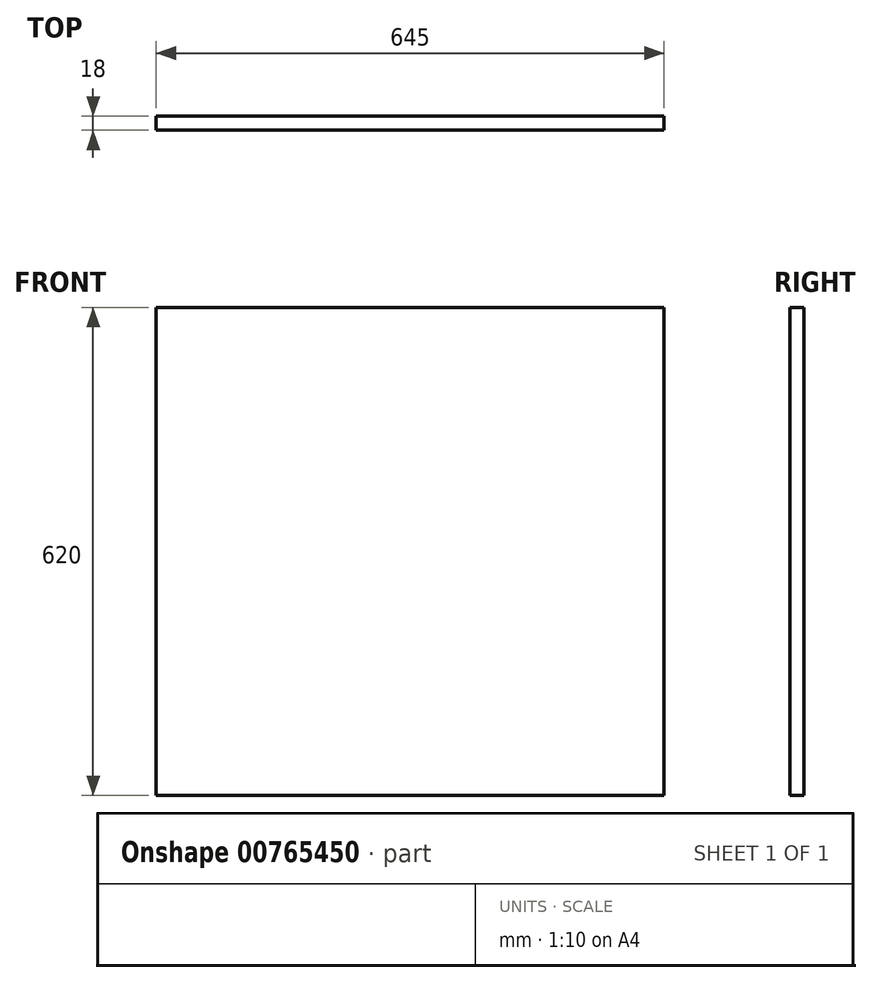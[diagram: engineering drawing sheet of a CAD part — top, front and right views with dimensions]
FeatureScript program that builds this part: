
annotation { "Feature Type Name" : "Feature", "Feature Type Description" : "" }
export const myFeature = defineFeature(function(context is Context, id is Id, definition is map)
    precondition{}
    {
        {
            var Q0;
            Q0=qCreatedBy(makeId("Front.planeOp"),FACE);
            var sketch = newSketch(context, id + "F0", { "sketchPlane" : qUnion([Q0])});
            skLineSegment(sketch, "E0.bottom", {"start": v(-322.5, -310) * mm, "end": v(322.5, -310) * mm});
            skLineSegment(sketch, "E0.top", {"start": v(-322.5, 310) * mm, "end": v(322.5, 310) * mm});
            skLineSegment(sketch, "E0.left", {"start": v(-322.5, -310) * mm, "end": v(-322.5, 310) * mm});
            skLineSegment(sketch, "E0.right", {"start": v(322.5, -310) * mm, "end": v(322.5, 310) * mm});
            skPoint(sketch, "E0.middle", {"position": v(0, 0) * mm});
            skSolve(sketch);
        }
        {
            var Q0;
            Q0 = qSketchRegion(id + "F0", true);
            extrude(context, id + "F1", {"entities" : qUnion([Q0]), "depth" : 18 * mm, "offsetDistance" : 25 * mm});
        }
    });
